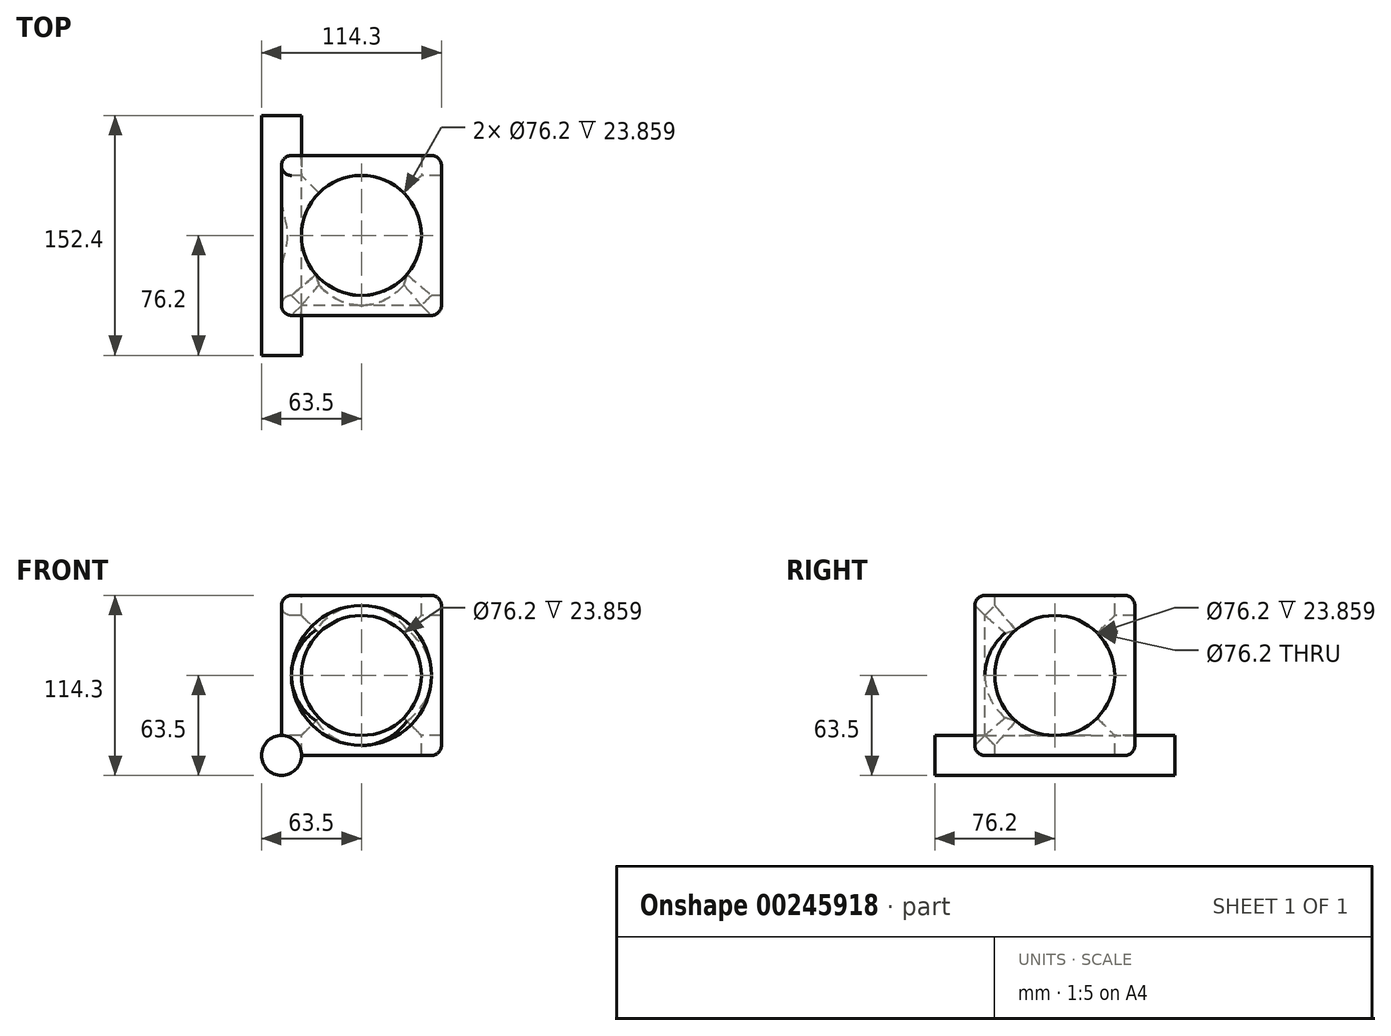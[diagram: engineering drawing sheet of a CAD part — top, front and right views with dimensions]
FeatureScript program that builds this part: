
annotation { "Feature Type Name" : "Feature", "Feature Type Description" : "" }
export const myFeature = defineFeature(function(context is Context, id is Id, definition is map)
    precondition{}
    {
        {
            var Q0;
            Q0=qCreatedBy(makeId("Front.planeOp"),FACE);
            var sketch = newSketch(context, id + "F0", { "sketchPlane" : qUnion([Q0])});
            skLineSegment(sketch, "E0", {"start": v(0, 0) * mm, "end": v(101.6, 0) * mm});
            skLineSegment(sketch, "E1", {"start": v(101.6, 0) * mm, "end": v(101.6, 101.6) * mm});
            skLineSegment(sketch, "E2", {"start": v(101.6, 101.6) * mm, "end": v(0, 101.6) * mm});
            skLineSegment(sketch, "E3", {"start": v(0, 101.6) * mm, "end": v(0, 0) * mm});
            skSolve(sketch);
        }
        {
            var Q0;
            Q0=makeQuery(id+"F0.imprint","IMPRINT",FACE,{"disambiguationData":[TD([[makeQuery(id+"F0.imprint","IMPRINT",EDGE,{"derivedFrom":sQuery(id+"F0.wireOp",EDGE,"E0")}),1.0]])]});
            extrude(context, id + "F1", {"entities" : qUnion([Q0]), "depth" : 101.6 * mm});
        }
        {
            var Q0;
            Q0=makeQuery(id+"F1.opExtrude","SWEPT_FACE",FACE,{"disambiguationData":[OSD([sQuery(id+"F0.wireOp",EDGE,"E2")])]});
            var sketch = newSketch(context, id + "F2", { "sketchPlane" : qUnion([Q0])});
            skCircle(sketch, "E4", {"center": v(50.8, -50.8) * mm, "radius": 38.1 * mm});
            skPoint(sketch, "E5.orphan", {"position": v(50.8, 0) * mm});
            skPoint(sketch, "E6.end.orphan", {"position": v(50.8, -101.6) * mm});
            skSolve(sketch);
        }
        {
            var Q0;
            Q0=makeQuery(id+"F2.imprint","IMPRINT",FACE,{"disambiguationData":[TD([[makeQuery(id+"F2.imprint","IMPRINT",EDGE,{"derivedFrom":sQuery(id+"F2.wireOp",EDGE,"E4")}),1.0]])]});
            extrude(context, id + "F3", {"entities" : qUnion([Q0]), "operationType" : NewBodyOperationType.REMOVE, "oppositeDirection" : true, "depth" : 101.6 * mm});
        }
        {
            var Q0;
            Q0=makeQuery(id+"F1.opExtrude","CAP_FACE",FACE,{"disambiguationData":[OSD([sQuery(id+"F0.wireOp",EDGE,"E0"),sQuery(id+"F0.wireOp",EDGE,"E1"),sQuery(id+"F0.wireOp",EDGE,"E2"),sQuery(id+"F0.wireOp",EDGE,"E3")])],"isStart":false});
            var sketch = newSketch(context, id + "F4", { "sketchPlane" : qUnion([Q0])});
            skCircle(sketch, "E7", {"center": v(50.8, 50.8) * mm, "radius": 38.1 * mm});
            skPoint(sketch, "E8.orphan", {"position": v(50.8, 101.6) * mm});
            skPoint(sketch, "E9.end.orphan", {"position": v(50.8, 0) * mm});
            skSolve(sketch);
        }
        {
            var Q0;
            Q0=makeQuery(id+"F4.imprint","IMPRINT",FACE,{"disambiguationData":[TD([[makeQuery(id+"F4.imprint","IMPRINT",EDGE,{"derivedFrom":sQuery(id+"F4.wireOp",EDGE,"E7")}),1.0]])]});
            extrude(context, id + "F5", {"entities" : qUnion([Q0]), "operationType" : NewBodyOperationType.REMOVE, "oppositeDirection" : true, "depth" : 101.6 * mm});
        }
        {
            var Q0;
            Q0=makeQuery(id+"F1.opExtrude","SWEPT_FACE",FACE,{"disambiguationData":[OSD([sQuery(id+"F0.wireOp",EDGE,"E3")])]});
            var sketch = newSketch(context, id + "F6", { "sketchPlane" : qUnion([Q0])});
            skCircle(sketch, "E10", {"center": v(50.8, 50.8) * mm, "radius": 38.1 * mm});
            skPoint(sketch, "E11.orphan", {"position": v(50.8, 101.6) * mm});
            skPoint(sketch, "E12.end.orphan", {"position": v(50.8, 0) * mm});
            skSolve(sketch);
        }
        {
            var Q0;
            Q0=makeQuery(id+"F6.imprint","IMPRINT",FACE,{"disambiguationData":[TD([[makeQuery(id+"F6.imprint","IMPRINT",EDGE,{"derivedFrom":sQuery(id+"F6.wireOp",EDGE,"E10")}),1.0]])]});
            extrude(context, id + "F7", {"entities" : qUnion([Q0]), "operationType" : NewBodyOperationType.REMOVE, "oppositeDirection" : true, "depth" : 101.6 * mm});
        }
        {
            var Q0;
            Q0=makeQuery(id+"F1.opExtrude","SWEPT_EDGE",EDGE,{"disambiguationData":[OSD([sQuery(id+"F0.wireOp",EDGE,"E2"),sQuery(id+"F0.wireOp",EDGE,"E3")])]});
            var Q1;
            Q1=makeQuery(id+"F1.opExtrude","CAP_EDGE",EDGE,{"disambiguationData":[OSD([sQuery(id+"F0.wireOp",EDGE,"E2")])],"isStart":false});
            var Q2;
            Q2=makeQuery(id+"F1.opExtrude","SWEPT_EDGE",EDGE,{"disambiguationData":[OSD([sQuery(id+"F0.wireOp",EDGE,"E1"),sQuery(id+"F0.wireOp",EDGE,"E2")])]});
            var Q3;
            Q3=makeQuery(id+"F1.opExtrude","CAP_EDGE",EDGE,{"disambiguationData":[OSD([sQuery(id+"F0.wireOp",EDGE,"E2")])],"isStart":true});
            var Q4;
            Q4=makeQuery(id+"F1.opExtrude","CAP_EDGE",EDGE,{"disambiguationData":[OSD([sQuery(id+"F0.wireOp",EDGE,"E0")])],"isStart":false});
            var Q5;
            Q5=makeQuery(id+"F1.opExtrude","SWEPT_EDGE",EDGE,{"disambiguationData":[OSD([sQuery(id+"F0.wireOp",EDGE,"E0"),sQuery(id+"F0.wireOp",EDGE,"E1")])]});
            var Q6;
            Q6=makeQuery(id+"F1.opExtrude","CAP_EDGE",EDGE,{"disambiguationData":[OSD([sQuery(id+"F0.wireOp",EDGE,"E1")])],"isStart":false});
            var Q7;
            Q7=makeQuery(id+"F1.opExtrude","CAP_EDGE",EDGE,{"disambiguationData":[OSD([sQuery(id+"F0.wireOp",EDGE,"E3")])],"isStart":false});
            var Q8;
            Q8=makeQuery(id+"F1.opExtrude","CAP_EDGE",EDGE,{"disambiguationData":[OSD([sQuery(id+"F0.wireOp",EDGE,"E1")])],"isStart":true});
            var Q9;
            Q9=makeQuery(id+"F1.opExtrude","SWEPT_FACE",FACE,{"disambiguationData":[OSD([sQuery(id+"F0.wireOp",EDGE,"E3")])]});
            var Q10;
            Q10=makeQuery(id+"F1.opExtrude","CAP_EDGE",EDGE,{"disambiguationData":[OSD([sQuery(id+"F0.wireOp",EDGE,"E0")])],"isStart":true});
            fillet(context, id + "F8", {"entities" : qUnion([Q0, Q1, Q2, Q3, Q4, Q5, Q6, Q7, Q8, Q9, Q10]), "radius" : 6.35 * mm, "tangentPropagation" : true, "allowEdgeOverflow" : false});
        }
        {
            var Q0;
            Q0=makeQuery(id+"F3.boolean.opBoolean","COPY",EDGE,{"derivedFrom":makeQuery(id+"F3.opExtrude","CAP_EDGE",EDGE,{"disambiguationData":[OSD([sQuery(id+"F2.wireOp",EDGE,"E4")])],"isStart":true})});
            var Q1;
            {var subQ0=makeQuery(id+"F5.opExtrude","SWEPT_FACE",FACE,{"disambiguationData":[OSD([sQuery(id+"F4.wireOp",EDGE,"E7")])]});Q1=makeQuery(id+"F5.boolean.opBoolean","COPY",FACE,{"disambiguationData":[TD([makeQuery(id+"F1.opExtrude","CAP_FACE",FACE,{"disambiguationData":[OSD([sQuery(id+"F0.wireOp",EDGE,"E0"),sQuery(id+"F0.wireOp",EDGE,"E1"),sQuery(id+"F0.wireOp",EDGE,"E2"),sQuery(id+"F0.wireOp",EDGE,"E3")])],"isStart":false})])],"derivedFrom":subQ0});}
            var Q2;
            Q2=makeQuery(id+"F7.boolean.opBoolean","COPY",EDGE,{"derivedFrom":makeQuery(id+"F7.opExtrude","CAP_EDGE",EDGE,{"disambiguationData":[OSD([sQuery(id+"F6.wireOp",EDGE,"E10")])],"isStart":false})});
            var Q3;
            Q3=makeQuery(id+"F3.boolean.opBoolean","COPY",EDGE,{"derivedFrom":makeQuery(id+"F3.opExtrude","CAP_EDGE",EDGE,{"disambiguationData":[OSD([sQuery(id+"F2.wireOp",EDGE,"E4")])],"isStart":false})});
            var Q4;
            Q4=makeQuery(id+"F5.boolean.opBoolean","COPY",EDGE,{"derivedFrom":makeQuery(id+"F5.opExtrude","CAP_EDGE",EDGE,{"disambiguationData":[OSD([sQuery(id+"F4.wireOp",EDGE,"E7")])],"isStart":false})});
            var Q5;
            Q5=makeQuery(id+"F8.opFillet","BLEND_FACE",FACE,{"disambiguationData":[OSD([sQuery(id+"F6.wireOp",EDGE,"E10")])]});
            chamfer(context, id + "F9", {"entities" : qUnion([Q0, Q1, Q2, Q3, Q4, Q5]), "width" : 6.35 * mm, "tangentPropagation" : true});
        }
        {
            var Q0;
            Q0=qCreatedBy(makeId("Front.planeOp"),FACE);
            cPlane(context, id + "F10", {"entities" : qUnion([Q0]), "cplaneType" : CPlaneType.OFFSET, "offset" : 101.6 * mm, "width" : 152.4 * mm, "height" : 152.4 * mm});
        }
        {
            var Q0;
            Q0=qCreatedBy(id+"F10.planeOp",FACE);
            var sketch = newSketch(context, id + "F11", { "sketchPlane" : qUnion([Q0])});
            skCircle(sketch, "E13", {"center": v(0, 0) * mm, "radius": 12.7 * mm});
            skSolve(sketch);
        }
        {
            var Q0;
            Q0=makeQuery(id+"F11.imprint","IMPRINT",FACE,{"disambiguationData":[TD([[makeQuery(id+"F11.imprint","IMPRINT",EDGE,{"derivedFrom":sQuery(id+"F11.wireOp",EDGE,"E13")}),1.0]])]});
            extrude(context, id + "F12", {"entities" : qUnion([Q0]), "operationType" : NewBodyOperationType.ADD, "depth" : 25.4 * mm, "hasSecondDirection" : true, "secondDirectionOppositeDirection" : true, "secondDirectionDepth" : 127 * mm});
        }
    });
